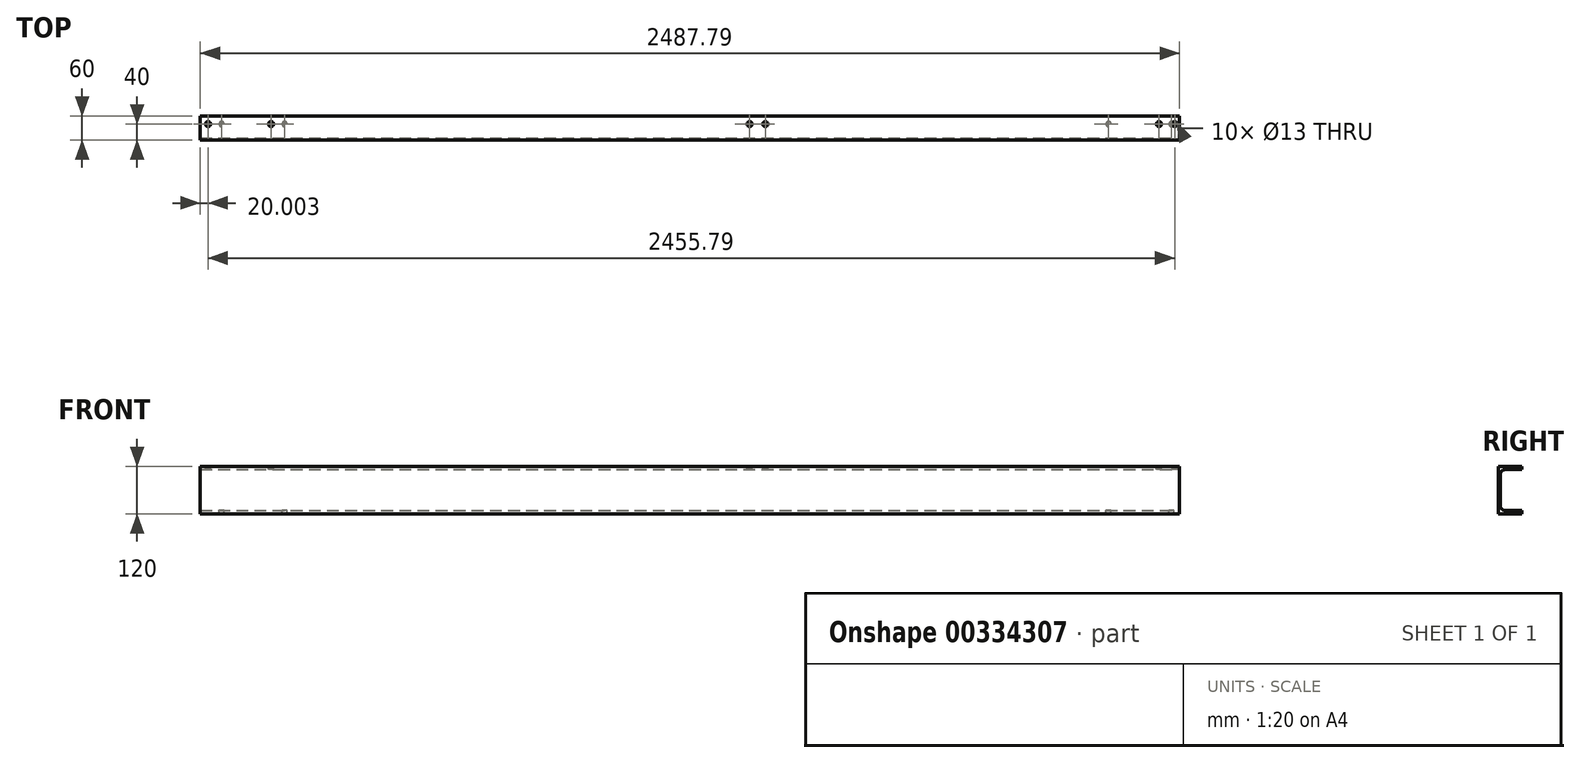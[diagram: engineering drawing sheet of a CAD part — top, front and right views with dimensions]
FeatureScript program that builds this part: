
annotation { "Feature Type Name" : "Feature", "Feature Type Description" : "" }
export const myFeature = defineFeature(function(context is Context, id is Id, definition is map)
    precondition{}
    {
        {
            assignVariable(context, id + "F0", {"name" : "L_Pro", "anyValue" : 2635 - 147.21});
        }
        {
            assignVariable(context, id + "F1", {"name" : "L_Hoe", "anyValue" : 120});
        }
        {
            var Q0;
            Q0=qCreatedBy(makeId("Right.planeOp"),FACE);
            var sketch = newSketch(context, id + "F2", { "sketchPlane" : qUnion([Q0])});
            skLineSegment(sketch, "E0", {"start": v(0, 0) * mm, "end": v(-60, 0) * mm});
            skLineSegment(sketch, "E1", {"start": v(-60, 0) * mm, "end": v(-60, 120) * mm});
            skLineSegment(sketch, "E2", {"start": v(-60, 120) * mm, "end": v(0, 120) * mm});
            skLineSegment(sketch, "E3", {"start": v(0, 120) * mm, "end": v(0, 112) * mm});
            skLineSegment(sketch, "E4", {"start": v(0, 112) * mm, "end": v(-43, 112) * mm});
            skLineSegment(sketch, "E5", {"start": v(-55, 100) * mm, "end": v(-55, 20) * mm});
            skLineSegment(sketch, "E6", {"start": v(-43, 8) * mm, "end": v(0, 8) * mm});
            skLineSegment(sketch, "E7", {"start": v(0, 8) * mm, "end": v(0, 0) * mm});
            skPoint(sketch, "E8.visualSharp", {"position": v(-55, 112) * mm});
            skArc(sketch, "E8.filletArc", {"start": v(-43, 112) * mm, "mid": v(-51.49, 108.49) * mm, "end": v(-55, 100) * mm});
            skPoint(sketch, "E9.visualSharp", {"position": v(-55, 8) * mm});
            skArc(sketch, "E9.filletArc", {"start": v(-55, 20) * mm, "mid": v(-51.49, 11.51) * mm, "end": v(-43, 8) * mm});
            skSolve(sketch);
        }
        {
            var Q0;
            Q0=qSketchRegion(id+"F2",true);
            var Q1;
            Q1=qConstructionFilter(qBodyType(qCreatedBy(id+"F2",EDGE),BodyType.WIRE),ConstructionObject.NO);
            extrude(context, id + "F3", {"entities" : qUnion([Q0]), "surfaceEntities" : qUnion([Q1]), "oppositeDirection" : true, "depth" : (getVariable(context, 'L_Pro')) * mm});
        }
        {
            var Q0;
            Q0=makeQuery(id+"F3.opExtrude","SWEPT_FACE",FACE,{"disambiguationData":[OSD([sQuery(id+"F2.wireOp",EDGE,"E6")])]});
            var sketch = newSketch(context, id + "F4", { "sketchPlane" : qUnion([Q0])});
            skCircle(sketch, "E10", {"center": v(-20, -20) * mm, "radius": 6.5 * mm});
            skCircle(sketch, "E11", {"center": v(-180, -20) * mm, "radius": 6.5 * mm});
            skCircle(sketch, "E12", {"center": v(-2433.38, -20) * mm, "radius": 6.5 * mm});
            skCircle(sketch, "E13", {"center": v(-2273.38, -20) * mm, "radius": 6.5 * mm});
            skSolve(sketch);
        }
        {
            var Q0;
            Q0=makeQuery(id+"F4.imprint","IMPRINT",FACE,{"disambiguationData":[TD([[makeQuery(id+"F4.imprint","IMPRINT",EDGE,{"derivedFrom":sQuery(id+"F4.wireOp",EDGE,"E13")}),1.0]])]});
            var Q1;
            Q1=makeQuery(id+"F4.imprint","IMPRINT",FACE,{"disambiguationData":[TD([[makeQuery(id+"F4.imprint","IMPRINT",EDGE,{"derivedFrom":sQuery(id+"F4.wireOp",EDGE,"E12")}),1.0]])]});
            extrude(context, id + "F5", {"entities" : qUnion([Q0, Q1]), "operationType" : NewBodyOperationType.REMOVE, "endBound" : BoundingType.UP_TO_NEXT, "oppositeDirection" : true, "depth" : (2 * getVariable(context, 'L_Hoe')) * mm});
        }
        {
            var Q0;
            Q0=makeQuery(id+"F3.opExtrude","SWEPT_FACE",FACE,{"disambiguationData":[OSD([sQuery(id+"F2.wireOp",EDGE,"E2")])]});
            var sketch = newSketch(context, id + "F6", { "sketchPlane" : qUnion([Q0])});
            skCircle(sketch, "E14", {"center": v(-12, -20) * mm, "radius": 6.5 * mm});
            skCircle(sketch, "E15", {"center": v(-52, -20) * mm, "radius": 6.5 * mm});
            skCircle(sketch, "E16", {"center": v(-1052, -20) * mm, "radius": 6.5 * mm});
            skCircle(sketch, "E17", {"center": v(-1092, -20) * mm, "radius": 6.5 * mm});
            skCircle(sketch, "E18", {"center": v(-2225.79, -20) * mm, "radius": 6.5 * mm});
            skCircle(sketch, "E19", {"center": v(-2265.79, -20) * mm, "radius": 6.5 * mm});
            skCircle(sketch, "E20", {"center": v(-180, -20) * mm, "radius": 6.5 * mm});
            skCircle(sketch, "E21", {"center": v(-340, -20) * mm, "radius": 6.5 * mm});
            skCircle(sketch, "E22", {"center": v(-2307.79, -20) * mm, "radius": 6.5 * mm});
            skCircle(sketch, "E23", {"center": v(-2467.79, -20) * mm, "radius": 6.5 * mm});
            skSolve(sketch);
        }
        {
            var Q0;
            Q0=qSketchRegion(id+"F4",true);
            var Q1;
            Q1=makeQuery(id+"F3.opExtrude","SWEPT_FACE",FACE,{"disambiguationData":[OSD([sQuery(id+"F2.wireOp",EDGE,"E0")])]});
            var Q2;
            Q2=makeQuery(id+"F3.opExtrude","SWEPT_FACE",FACE,{"disambiguationData":[OSD([sQuery(id+"F2.wireOp",EDGE,"E0")])]});
            extrude(context, id + "F7", {"entities" : qUnion([Q0, Q1]), "operationType" : NewBodyOperationType.REMOVE, "endBound" : BoundingType.THROUGH_ALL, "oppositeDirection" : true, "endBoundEntityFace" : qUnion([Q2]), "depth" : 25 * mm});
        }
        {
            var Q0;
            Q0=makeQuery(id+"F6.imprint","IMPRINT",FACE,{"disambiguationData":[TD([[makeQuery(id+"F6.imprint","IMPRINT",EDGE,{"derivedFrom":sQuery(id+"F6.wireOp",EDGE,"E15")}),1.0]])]});
            var Q1;
            Q1=makeQuery(id+"F6.imprint","IMPRINT",FACE,{"disambiguationData":[TD([[makeQuery(id+"F6.imprint","IMPRINT",EDGE,{"derivedFrom":sQuery(id+"F6.wireOp",EDGE,"E14")}),1.0]])]});
            var Q2;
            Q2=makeQuery(id+"F6.imprint","IMPRINT",FACE,{"disambiguationData":[TD([[makeQuery(id+"F6.imprint","IMPRINT",EDGE,{"derivedFrom":sQuery(id+"F6.wireOp",EDGE,"E16")}),1.0]])]});
            var Q3;
            Q3=makeQuery(id+"F6.imprint","IMPRINT",FACE,{"disambiguationData":[TD([[makeQuery(id+"F6.imprint","IMPRINT",EDGE,{"derivedFrom":sQuery(id+"F6.wireOp",EDGE,"E17")}),1.0]])]});
            var Q4;
            Q4=makeQuery(id+"F6.imprint","IMPRINT",FACE,{"disambiguationData":[TD([[makeQuery(id+"F6.imprint","IMPRINT",EDGE,{"derivedFrom":sQuery(id+"F6.wireOp",EDGE,"E22")}),1.0]])]});
            var Q5;
            Q5=makeQuery(id+"F6.imprint","IMPRINT",FACE,{"disambiguationData":[TD([[makeQuery(id+"F6.imprint","IMPRINT",EDGE,{"derivedFrom":sQuery(id+"F6.wireOp",EDGE,"E23")}),1.0]])]});
            extrude(context, id + "F8", {"entities" : qUnion([Q0, Q1, Q2, Q3, Q4, Q5]), "operationType" : NewBodyOperationType.REMOVE, "endBound" : BoundingType.UP_TO_NEXT, "oppositeDirection" : true, "depth" : 25 * mm});
        }
    });
